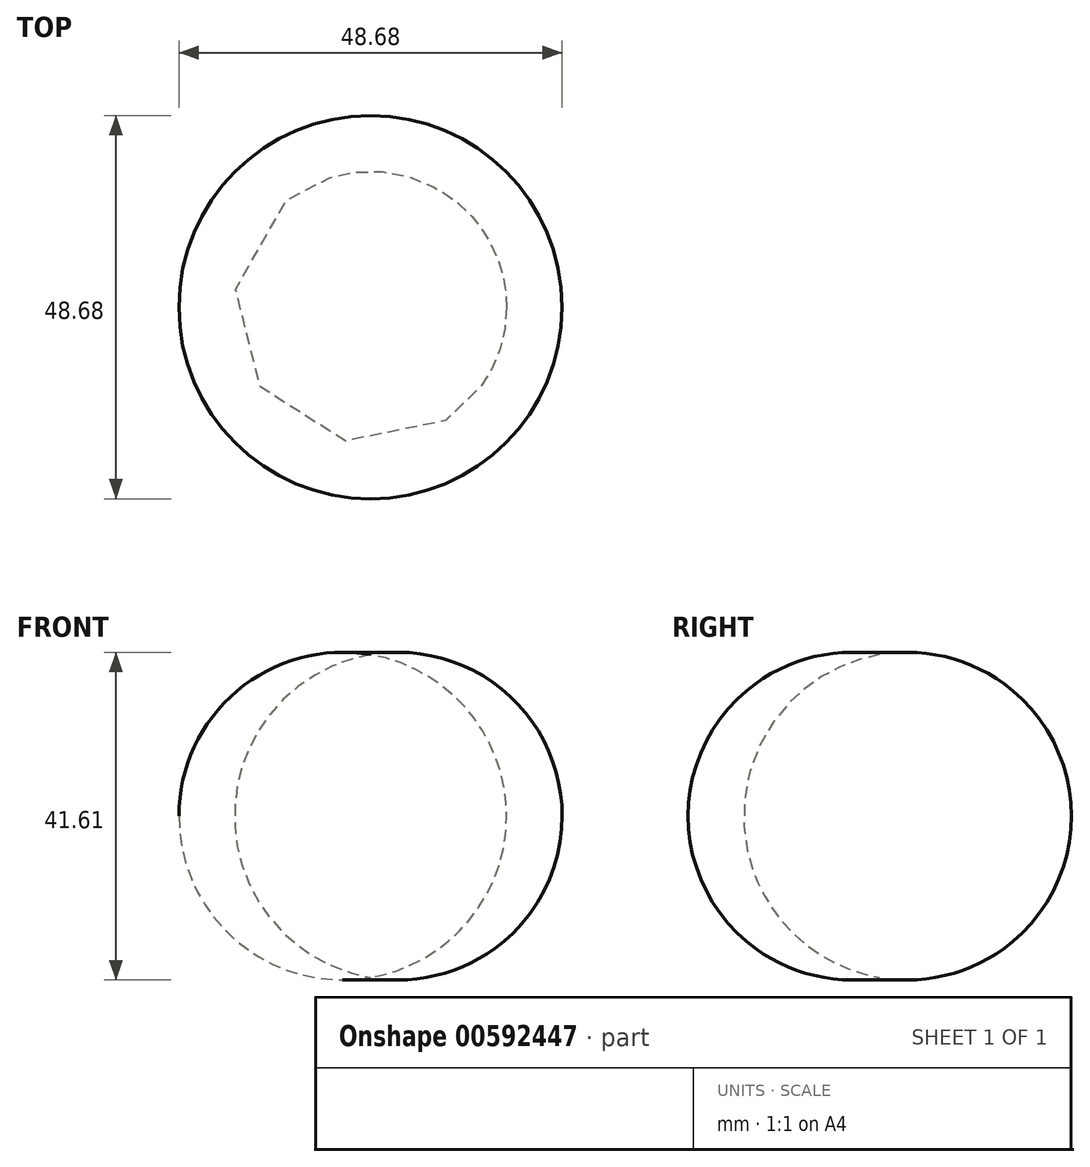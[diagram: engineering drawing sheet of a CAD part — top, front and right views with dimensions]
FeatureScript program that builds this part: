
annotation { "Feature Type Name" : "Feature", "Feature Type Description" : "" }
export const myFeature = defineFeature(function(context is Context, id is Id, definition is map)
    precondition{}
    {
        {
            var Q0;
            Q0=qCreatedBy(makeId("Front.planeOp"),FACE);
            var sketch = newSketch(context, id + "F0", { "sketchPlane" : qUnion([Q0])});
            skLineSegment(sketch, "E0", {"start": v(0, 0) * mm, "end": v(0, 41.01) * mm});
            skArc(sketch, "E1", {"start": v(0, 0) * mm, "mid": v(24.34, 20.5) * mm, "end": v(0, 41.01) * mm});
            skSolve(sketch);
        }
        {
            var Q0;
            Q0=makeQuery(id+"F0.imprint","IMPRINT",FACE,{"disambiguationData":[TD([[makeQuery(id+"F0.imprint","IMPRINT",EDGE,{"derivedFrom":sQuery(id+"F0.wireOp",EDGE,"E0")}),-1.0]])]});
            var Q1;
            Q1=sQuery(id+"F0.wireOp",EDGE,"E0");
            revolve(context, id + "F1", {"entities" : qUnion([Q0]), "axis" : qUnion([Q1]), "revolveType" : RevolveType.FULL});
        }
    });
